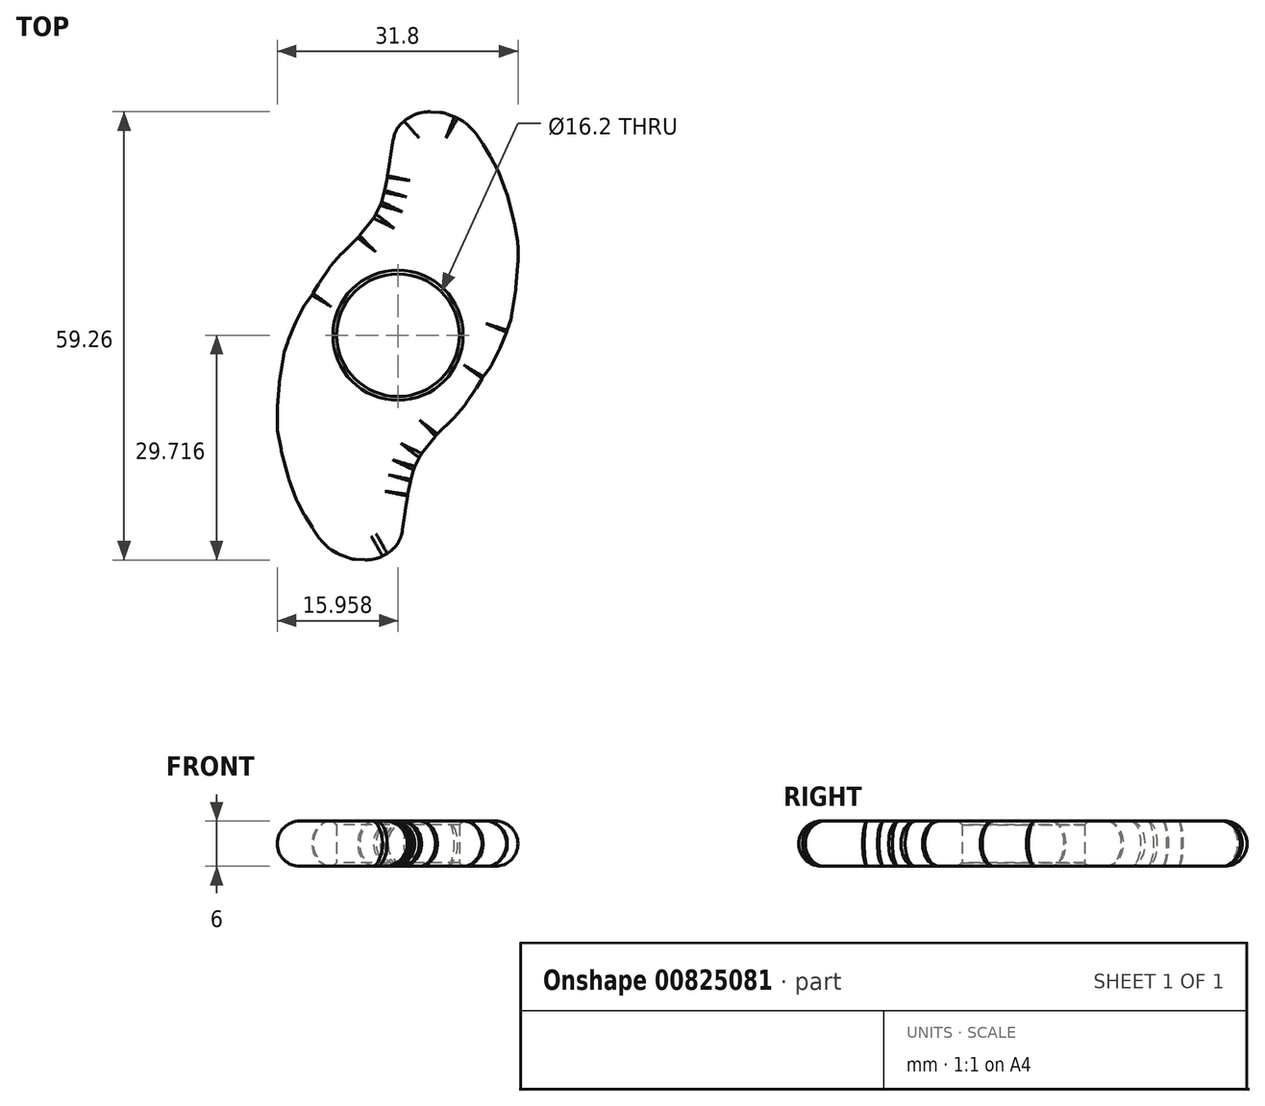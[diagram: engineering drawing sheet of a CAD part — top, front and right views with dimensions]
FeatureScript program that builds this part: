
annotation { "Feature Type Name" : "Feature", "Feature Type Description" : "" }
export const myFeature = defineFeature(function(context is Context, id is Id, definition is map)
    precondition{}
    {
        {
            var Q0;
            Q0=qCreatedBy(makeId("Top.planeOp"),FACE);
            var sketch = newSketch(context, id + "F0", { "sketchPlane" : qUnion([Q0])});
            skLineSegment(sketch, "E0", {"start": v(11.23, -5.5) * mm, "end": v(-11.23, 5.5) * mm});
            skLineSegment(sketch, "E1", {"start": v(11.23, -5.5) * mm, "end": v(12.39, -3.95) * mm});
            skLineSegment(sketch, "E2", {"start": v(12.39, -3.95) * mm, "end": v(13.48, -1.7) * mm});
            skLineSegment(sketch, "E3", {"start": v(13.48, -1.7) * mm, "end": v(14.46, 0.6) * mm});
            skLineSegment(sketch, "E4", {"start": v(14.46, 0.6) * mm, "end": v(15.04, 2.4) * mm});
            skLineSegment(sketch, "E5", {"start": v(15.04, 2.4) * mm, "end": v(15.61, 6.2) * mm});
            skLineSegment(sketch, "E6", {"start": v(15.61, 6.2) * mm, "end": v(15.9, 9.53) * mm});
            skLineSegment(sketch, "E7", {"start": v(15.9, 9.53) * mm, "end": v(15.9, 12.24) * mm});
            skLineSegment(sketch, "E8", {"start": v(15.9, 12.24) * mm, "end": v(15.38, 15.12) * mm});
            skLineSegment(sketch, "E9", {"start": v(15.38, 15.12) * mm, "end": v(14.4, 18.87) * mm});
            skLineSegment(sketch, "E10", {"start": v(14.4, 18.87) * mm, "end": v(13.3, 21.8) * mm});
            skLineSegment(sketch, "E11", {"start": v(13.3, 21.8) * mm, "end": v(12.27, 23.7) * mm});
            skLineSegment(sketch, "E12", {"start": v(12.27, 23.7) * mm, "end": v(11.23, 25.44) * mm});
            skLineSegment(sketch, "E13", {"start": v(11.23, 25.44) * mm, "end": v(10.25, 26.88) * mm});
            skLineSegment(sketch, "E14", {"start": v(10.25, 26.88) * mm, "end": v(9.1, 28.09) * mm});
            skLineSegment(sketch, "E15", {"start": v(9.1, 28.09) * mm, "end": v(7.72, 28.9) * mm});
            skLineSegment(sketch, "E16", {"start": v(7.72, 28.9) * mm, "end": v(6.05, 29.53) * mm});
            skLineSegment(sketch, "E17", {"start": v(6.05, 29.53) * mm, "end": v(3.92, 29.64) * mm});
            skLineSegment(sketch, "E18", {"start": v(3.92, 29.64) * mm, "end": v(2.42, 29.35) * mm});
            skLineSegment(sketch, "E19", {"start": v(2.42, 29.35) * mm, "end": v(1.1, 28.6) * mm});
            skLineSegment(sketch, "E20", {"start": v(1.1, 28.6) * mm, "end": v(0.12, 27.74) * mm});
            skLineSegment(sketch, "E21", {"start": v(0.12, 27.74) * mm, "end": v(-0.4, 26.7) * mm});
            skLineSegment(sketch, "E22", {"start": v(-0.4, 26.7) * mm, "end": v(-0.63, 25.78) * mm});
            skLineSegment(sketch, "E23", {"start": v(-0.63, 25.78) * mm, "end": v(-1.04, 23.13) * mm});
            skLineSegment(sketch, "E24", {"start": v(-1.04, 23.13) * mm, "end": v(-1.33, 21.06) * mm});
            skLineSegment(sketch, "E25", {"start": v(-1.33, 21.06) * mm, "end": v(-1.73, 19.1) * mm});
            skLineSegment(sketch, "E26", {"start": v(-1.73, 19.1) * mm, "end": v(-2.19, 17.48) * mm});
            skLineSegment(sketch, "E27", {"start": v(-2.19, 17.48) * mm, "end": v(-3, 15.81) * mm});
            skLineSegment(sketch, "E28", {"start": v(-3, 15.81) * mm, "end": v(-5.13, 13.1) * mm});
            skLineSegment(sketch, "E29", {"start": v(-5.13, 13.1) * mm, "end": v(-7.43, 10.86) * mm});
            skLineSegment(sketch, "E30", {"start": v(-7.43, 10.86) * mm, "end": v(-8.93, 9.13) * mm});
            skLineSegment(sketch, "E31", {"start": v(-8.93, 9.13) * mm, "end": v(-10.37, 6.94) * mm});
            skLineSegment(sketch, "E32", {"start": v(-10.37, 6.94) * mm, "end": v(-11.23, 5.5) * mm});
            skLineSegment(sketch, "E33", {"start": v(-11.23, 5.5) * mm, "end": v(-12.39, 3.95) * mm});
            skLineSegment(sketch, "E34", {"start": v(-12.39, 3.95) * mm, "end": v(-13.48, 1.7) * mm});
            skLineSegment(sketch, "E35", {"start": v(-13.48, 1.7) * mm, "end": v(-14.46, -0.6) * mm});
            skLineSegment(sketch, "E36", {"start": v(-14.46, -0.6) * mm, "end": v(-15.04, -2.4) * mm});
            skLineSegment(sketch, "E37", {"start": v(-15.04, -2.4) * mm, "end": v(-15.61, -6.2) * mm});
            skLineSegment(sketch, "E38", {"start": v(-15.61, -6.2) * mm, "end": v(-15.9, -9.53) * mm});
            skLineSegment(sketch, "E39", {"start": v(-15.9, -9.53) * mm, "end": v(-15.9, -12.24) * mm});
            skLineSegment(sketch, "E40", {"start": v(-15.9, -12.24) * mm, "end": v(-15.38, -15.12) * mm});
            skLineSegment(sketch, "E41", {"start": v(-15.38, -15.12) * mm, "end": v(-14.4, -18.87) * mm});
            skLineSegment(sketch, "E42", {"start": v(-14.4, -18.87) * mm, "end": v(-13.3, -21.8) * mm});
            skLineSegment(sketch, "E43", {"start": v(-13.3, -21.8) * mm, "end": v(-12.27, -23.7) * mm});
            skLineSegment(sketch, "E44", {"start": v(-12.27, -23.7) * mm, "end": v(-11.23, -25.44) * mm});
            skLineSegment(sketch, "E45", {"start": v(-11.23, -25.44) * mm, "end": v(-10.25, -26.88) * mm});
            skLineSegment(sketch, "E46", {"start": v(-10.25, -26.88) * mm, "end": v(-9.1, -28.09) * mm});
            skLineSegment(sketch, "E47", {"start": v(-9.1, -28.09) * mm, "end": v(-7.72, -28.9) * mm});
            skLineSegment(sketch, "E48", {"start": v(-7.72, -28.9) * mm, "end": v(-6.05, -29.53) * mm});
            skLineSegment(sketch, "E49", {"start": v(-6.05, -29.53) * mm, "end": v(-3.92, -29.64) * mm});
            skLineSegment(sketch, "E50", {"start": v(-3.92, -29.64) * mm, "end": v(-2.42, -29.35) * mm});
            skLineSegment(sketch, "E51", {"start": v(-2.42, -29.35) * mm, "end": v(-1.1, -28.6) * mm});
            skLineSegment(sketch, "E52", {"start": v(-1.1, -28.6) * mm, "end": v(-0.12, -27.74) * mm});
            skLineSegment(sketch, "E53", {"start": v(-0.12, -27.74) * mm, "end": v(0.4, -26.7) * mm});
            skLineSegment(sketch, "E54", {"start": v(0.4, -26.7) * mm, "end": v(0.63, -25.78) * mm});
            skLineSegment(sketch, "E55", {"start": v(0.63, -25.78) * mm, "end": v(1.04, -23.13) * mm});
            skLineSegment(sketch, "E56", {"start": v(1.04, -23.13) * mm, "end": v(1.33, -21.06) * mm});
            skLineSegment(sketch, "E57", {"start": v(1.33, -21.06) * mm, "end": v(1.73, -19.1) * mm});
            skLineSegment(sketch, "E58", {"start": v(1.73, -19.1) * mm, "end": v(2.19, -17.48) * mm});
            skLineSegment(sketch, "E59", {"start": v(2.19, -17.48) * mm, "end": v(3, -15.81) * mm});
            skLineSegment(sketch, "E60", {"start": v(3, -15.81) * mm, "end": v(5.13, -13.1) * mm});
            skLineSegment(sketch, "E61", {"start": v(5.13, -13.1) * mm, "end": v(7.43, -10.86) * mm});
            skLineSegment(sketch, "E62", {"start": v(7.43, -10.86) * mm, "end": v(8.93, -9.13) * mm});
            skLineSegment(sketch, "E63", {"start": v(8.93, -9.13) * mm, "end": v(10.37, -6.94) * mm});
            skLineSegment(sketch, "E64", {"start": v(10.37, -6.94) * mm, "end": v(11.23, -5.5) * mm});
            skLineSegment(sketch, "E65", {"start": v(0.06, 0.09) * mm, "end": v(-0.46, -1.07) * mm});
            skCircle(sketch, "E66", {"center": v(0.06, 0.09) * mm, "radius": 8.1 * mm});
            skSolve(sketch);
        }
        {
            var Q0;
            Q0 = qSketchRegion(id + "F0", true);
            var Q1;
            {var subQ0=sQuery(id+"F0.wireOp",EDGE,"E1");Q1=makeQuery(id+"F0.imprint","IMPRINT",FACE,{"disambiguationData":[TD([[makeQuery(id+"F0.imprint","IMPRINT",EDGE,{"derivedFrom":subQ0}),1.0]])]});}
            extrude(context, id + "F1", {"entities" : qUnion([Q0, Q1]), "depth" : 6 * mm, "offsetDistance" : 25 * mm});
        }
        {
            var Q0;
            Q0=makeQuery(id+"F1.opExtrude","CAP_EDGE",EDGE,{"disambiguationData":[OSD([sQuery(id+"F0.wireOp",EDGE,"E66")])],"isStart":false});
            var Q1;
            Q1=makeQuery(id+"F1.opExtrude","CAP_EDGE",EDGE,{"disambiguationData":[OSD([sQuery(id+"F0.wireOp",EDGE,"E66")])],"isStart":true});
            chamfer(context, id + "F2", {"entities" : qUnion([Q0, Q1]), "width" : 0.5 * mm, "tangentPropagation" : true});
        }
        {
            var Q0;
            Q0=makeQuery(id+"F1.opExtrude","CAP_EDGE",EDGE,{"disambiguationData":[OSD([sQuery(id+"F0.wireOp",EDGE,"E60")])],"isStart":false});
            var Q1;
            Q1=makeQuery(id+"F1.opExtrude","CAP_EDGE",EDGE,{"disambiguationData":[OSD([sQuery(id+"F0.wireOp",EDGE,"E61")])],"isStart":false});
            var Q2;
            Q2=makeQuery(id+"F1.opExtrude","CAP_EDGE",EDGE,{"disambiguationData":[OSD([sQuery(id+"F0.wireOp",EDGE,"E62")])],"isStart":false});
            var Q3;
            Q3=makeQuery(id+"F1.opExtrude","CAP_EDGE",EDGE,{"disambiguationData":[OSD([sQuery(id+"F0.wireOp",EDGE,"E63")])],"isStart":false});
            var Q4;
            Q4=makeQuery(id+"F1.opExtrude","CAP_EDGE",EDGE,{"disambiguationData":[OSD([sQuery(id+"F0.wireOp",EDGE,"E64")])],"isStart":false});
            var Q5;
            Q5=makeQuery(id+"F1.opExtrude","CAP_EDGE",EDGE,{"disambiguationData":[OSD([sQuery(id+"F0.wireOp",EDGE,"E1")])],"isStart":false});
            var Q6;
            Q6=makeQuery(id+"F1.opExtrude","CAP_EDGE",EDGE,{"disambiguationData":[OSD([sQuery(id+"F0.wireOp",EDGE,"E2")])],"isStart":false});
            var Q7;
            Q7=makeQuery(id+"F1.opExtrude","CAP_EDGE",EDGE,{"disambiguationData":[OSD([sQuery(id+"F0.wireOp",EDGE,"E3")])],"isStart":false});
            var Q8;
            Q8=makeQuery(id+"F1.opExtrude","CAP_EDGE",EDGE,{"disambiguationData":[OSD([sQuery(id+"F0.wireOp",EDGE,"E4")])],"isStart":false});
            var Q9;
            Q9=makeQuery(id+"F1.opExtrude","CAP_EDGE",EDGE,{"disambiguationData":[OSD([sQuery(id+"F0.wireOp",EDGE,"E5")])],"isStart":false});
            var Q10;
            Q10=makeQuery(id+"F1.opExtrude","CAP_EDGE",EDGE,{"disambiguationData":[OSD([sQuery(id+"F0.wireOp",EDGE,"E6")])],"isStart":false});
            var Q11;
            Q11=makeQuery(id+"F1.opExtrude","CAP_EDGE",EDGE,{"disambiguationData":[OSD([sQuery(id+"F0.wireOp",EDGE,"E7")])],"isStart":false});
            var Q12;
            Q12=makeQuery(id+"F1.opExtrude","CAP_EDGE",EDGE,{"disambiguationData":[OSD([sQuery(id+"F0.wireOp",EDGE,"E8")])],"isStart":false});
            var Q13;
            Q13=makeQuery(id+"F1.opExtrude","CAP_EDGE",EDGE,{"disambiguationData":[OSD([sQuery(id+"F0.wireOp",EDGE,"E9")])],"isStart":false});
            var Q14;
            Q14=makeQuery(id+"F1.opExtrude","CAP_EDGE",EDGE,{"disambiguationData":[OSD([sQuery(id+"F0.wireOp",EDGE,"E10")])],"isStart":false});
            var Q15;
            Q15=makeQuery(id+"F1.opExtrude","CAP_EDGE",EDGE,{"disambiguationData":[OSD([sQuery(id+"F0.wireOp",EDGE,"E11")])],"isStart":false});
            var Q16;
            Q16=makeQuery(id+"F1.opExtrude","CAP_EDGE",EDGE,{"disambiguationData":[OSD([sQuery(id+"F0.wireOp",EDGE,"E12")])],"isStart":false});
            var Q17;
            Q17=makeQuery(id+"F1.opExtrude","CAP_EDGE",EDGE,{"disambiguationData":[OSD([sQuery(id+"F0.wireOp",EDGE,"E13")])],"isStart":false});
            var Q18;
            Q18=makeQuery(id+"F1.opExtrude","CAP_EDGE",EDGE,{"disambiguationData":[OSD([sQuery(id+"F0.wireOp",EDGE,"E14")])],"isStart":false});
            var Q19;
            Q19=makeQuery(id+"F1.opExtrude","CAP_EDGE",EDGE,{"disambiguationData":[OSD([sQuery(id+"F0.wireOp",EDGE,"E15")])],"isStart":false});
            var Q20;
            Q20=makeQuery(id+"F1.opExtrude","CAP_EDGE",EDGE,{"disambiguationData":[OSD([sQuery(id+"F0.wireOp",EDGE,"E16")])],"isStart":false});
            var Q21;
            Q21=makeQuery(id+"F1.opExtrude","CAP_EDGE",EDGE,{"disambiguationData":[OSD([sQuery(id+"F0.wireOp",EDGE,"E17")])],"isStart":false});
            var Q22;
            Q22=makeQuery(id+"F1.opExtrude","CAP_EDGE",EDGE,{"disambiguationData":[OSD([sQuery(id+"F0.wireOp",EDGE,"E59")])],"isStart":false});
            var Q23;
            Q23=makeQuery(id+"F1.opExtrude","CAP_EDGE",EDGE,{"disambiguationData":[OSD([sQuery(id+"F0.wireOp",EDGE,"E58")])],"isStart":false});
            var Q24;
            Q24=makeQuery(id+"F1.opExtrude","CAP_EDGE",EDGE,{"disambiguationData":[OSD([sQuery(id+"F0.wireOp",EDGE,"E49")])],"isStart":false});
            var Q25;
            Q25=makeQuery(id+"F1.opExtrude","CAP_EDGE",EDGE,{"disambiguationData":[OSD([sQuery(id+"F0.wireOp",EDGE,"E51")])],"isStart":false});
            var Q26;
            Q26=makeQuery(id+"F1.opExtrude","CAP_EDGE",EDGE,{"disambiguationData":[OSD([sQuery(id+"F0.wireOp",EDGE,"E50")])],"isStart":false});
            var Q27;
            Q27=makeQuery(id+"F1.opExtrude","CAP_EDGE",EDGE,{"disambiguationData":[OSD([sQuery(id+"F0.wireOp",EDGE,"E52")])],"isStart":false});
            var Q28;
            Q28=makeQuery(id+"F1.opExtrude","CAP_EDGE",EDGE,{"disambiguationData":[OSD([sQuery(id+"F0.wireOp",EDGE,"E53")])],"isStart":false});
            var Q29;
            Q29=makeQuery(id+"F1.opExtrude","CAP_EDGE",EDGE,{"disambiguationData":[OSD([sQuery(id+"F0.wireOp",EDGE,"E54")])],"isStart":false});
            var Q30;
            Q30=makeQuery(id+"F1.opExtrude","CAP_EDGE",EDGE,{"disambiguationData":[OSD([sQuery(id+"F0.wireOp",EDGE,"E55")])],"isStart":false});
            var Q31;
            Q31=makeQuery(id+"F1.opExtrude","CAP_EDGE",EDGE,{"disambiguationData":[OSD([sQuery(id+"F0.wireOp",EDGE,"E56")])],"isStart":false});
            var Q32;
            Q32=makeQuery(id+"F1.opExtrude","CAP_EDGE",EDGE,{"disambiguationData":[OSD([sQuery(id+"F0.wireOp",EDGE,"E57")])],"isStart":false});
            var Q33;
            Q33=makeQuery(id+"F1.opExtrude","CAP_EDGE",EDGE,{"disambiguationData":[OSD([sQuery(id+"F0.wireOp",EDGE,"E48")])],"isStart":false});
            var Q34;
            Q34=makeQuery(id+"F1.opExtrude","CAP_EDGE",EDGE,{"disambiguationData":[OSD([sQuery(id+"F0.wireOp",EDGE,"E47")])],"isStart":false});
            var Q35;
            Q35=makeQuery(id+"F1.opExtrude","CAP_EDGE",EDGE,{"disambiguationData":[OSD([sQuery(id+"F0.wireOp",EDGE,"E46")])],"isStart":false});
            var Q36;
            Q36=makeQuery(id+"F1.opExtrude","CAP_EDGE",EDGE,{"disambiguationData":[OSD([sQuery(id+"F0.wireOp",EDGE,"E45")])],"isStart":false});
            var Q37;
            Q37=makeQuery(id+"F1.opExtrude","CAP_EDGE",EDGE,{"disambiguationData":[OSD([sQuery(id+"F0.wireOp",EDGE,"E44")])],"isStart":false});
            var Q38;
            Q38=makeQuery(id+"F1.opExtrude","CAP_EDGE",EDGE,{"disambiguationData":[OSD([sQuery(id+"F0.wireOp",EDGE,"E43")])],"isStart":false});
            var Q39;
            Q39=makeQuery(id+"F1.opExtrude","CAP_EDGE",EDGE,{"disambiguationData":[OSD([sQuery(id+"F0.wireOp",EDGE,"E42")])],"isStart":false});
            var Q40;
            Q40=makeQuery(id+"F1.opExtrude","CAP_EDGE",EDGE,{"disambiguationData":[OSD([sQuery(id+"F0.wireOp",EDGE,"E41")])],"isStart":false});
            var Q41;
            Q41=makeQuery(id+"F1.opExtrude","CAP_EDGE",EDGE,{"disambiguationData":[OSD([sQuery(id+"F0.wireOp",EDGE,"E40")])],"isStart":false});
            var Q42;
            Q42=makeQuery(id+"F1.opExtrude","CAP_EDGE",EDGE,{"disambiguationData":[OSD([sQuery(id+"F0.wireOp",EDGE,"E39")])],"isStart":false});
            var Q43;
            Q43=makeQuery(id+"F1.opExtrude","CAP_EDGE",EDGE,{"disambiguationData":[OSD([sQuery(id+"F0.wireOp",EDGE,"E38")])],"isStart":false});
            var Q44;
            Q44=makeQuery(id+"F1.opExtrude","CAP_EDGE",EDGE,{"disambiguationData":[OSD([sQuery(id+"F0.wireOp",EDGE,"E37")])],"isStart":false});
            var Q45;
            Q45=makeQuery(id+"F1.opExtrude","CAP_EDGE",EDGE,{"disambiguationData":[OSD([sQuery(id+"F0.wireOp",EDGE,"E36")])],"isStart":false});
            var Q46;
            Q46=makeQuery(id+"F1.opExtrude","CAP_EDGE",EDGE,{"disambiguationData":[OSD([sQuery(id+"F0.wireOp",EDGE,"E35")])],"isStart":false});
            var Q47;
            Q47=makeQuery(id+"F1.opExtrude","CAP_EDGE",EDGE,{"disambiguationData":[OSD([sQuery(id+"F0.wireOp",EDGE,"E34")])],"isStart":false});
            var Q48;
            Q48=makeQuery(id+"F1.opExtrude","CAP_EDGE",EDGE,{"disambiguationData":[OSD([sQuery(id+"F0.wireOp",EDGE,"E33")])],"isStart":false});
            var Q49;
            Q49=makeQuery(id+"F1.opExtrude","CAP_EDGE",EDGE,{"disambiguationData":[OSD([sQuery(id+"F0.wireOp",EDGE,"E32")])],"isStart":false});
            var Q50;
            Q50=makeQuery(id+"F1.opExtrude","CAP_EDGE",EDGE,{"disambiguationData":[OSD([sQuery(id+"F0.wireOp",EDGE,"E31")])],"isStart":false});
            var Q51;
            Q51=makeQuery(id+"F1.opExtrude","CAP_EDGE",EDGE,{"disambiguationData":[OSD([sQuery(id+"F0.wireOp",EDGE,"E30")])],"isStart":false});
            var Q52;
            Q52=makeQuery(id+"F1.opExtrude","CAP_EDGE",EDGE,{"disambiguationData":[OSD([sQuery(id+"F0.wireOp",EDGE,"E29")])],"isStart":false});
            var Q53;
            Q53=makeQuery(id+"F1.opExtrude","CAP_EDGE",EDGE,{"disambiguationData":[OSD([sQuery(id+"F0.wireOp",EDGE,"E28")])],"isStart":false});
            var Q54;
            Q54=makeQuery(id+"F1.opExtrude","CAP_EDGE",EDGE,{"disambiguationData":[OSD([sQuery(id+"F0.wireOp",EDGE,"E27")])],"isStart":false});
            var Q55;
            Q55=makeQuery(id+"F1.opExtrude","CAP_EDGE",EDGE,{"disambiguationData":[OSD([sQuery(id+"F0.wireOp",EDGE,"E26")])],"isStart":false});
            var Q56;
            Q56=makeQuery(id+"F1.opExtrude","CAP_EDGE",EDGE,{"disambiguationData":[OSD([sQuery(id+"F0.wireOp",EDGE,"E22")])],"isStart":false});
            var Q57;
            Q57=makeQuery(id+"F1.opExtrude","CAP_EDGE",EDGE,{"disambiguationData":[OSD([sQuery(id+"F0.wireOp",EDGE,"E21")])],"isStart":false});
            var Q58;
            Q58=makeQuery(id+"F1.opExtrude","CAP_EDGE",EDGE,{"disambiguationData":[OSD([sQuery(id+"F0.wireOp",EDGE,"E20")])],"isStart":false});
            var Q59;
            Q59=makeQuery(id+"F1.opExtrude","CAP_EDGE",EDGE,{"disambiguationData":[OSD([sQuery(id+"F0.wireOp",EDGE,"E19")])],"isStart":false});
            var Q60;
            Q60=makeQuery(id+"F1.opExtrude","CAP_EDGE",EDGE,{"disambiguationData":[OSD([sQuery(id+"F0.wireOp",EDGE,"E18")])],"isStart":false});
            var Q61;
            Q61=makeQuery(id+"F1.opExtrude","CAP_EDGE",EDGE,{"disambiguationData":[OSD([sQuery(id+"F0.wireOp",EDGE,"E25")])],"isStart":false});
            var Q62;
            Q62=makeQuery(id+"F1.opExtrude","CAP_EDGE",EDGE,{"disambiguationData":[OSD([sQuery(id+"F0.wireOp",EDGE,"E24")])],"isStart":false});
            var Q63;
            Q63=makeQuery(id+"F1.opExtrude","CAP_EDGE",EDGE,{"disambiguationData":[OSD([sQuery(id+"F0.wireOp",EDGE,"E23")])],"isStart":false});
            var Q64;
            Q64=makeQuery(id+"F1.opExtrude","CAP_EDGE",EDGE,{"disambiguationData":[OSD([sQuery(id+"F0.wireOp",EDGE,"E26")])],"isStart":true});
            var Q65;
            Q65=makeQuery(id+"F1.opExtrude","CAP_EDGE",EDGE,{"disambiguationData":[OSD([sQuery(id+"F0.wireOp",EDGE,"E25")])],"isStart":true});
            var Q66;
            Q66=makeQuery(id+"F1.opExtrude","CAP_EDGE",EDGE,{"disambiguationData":[OSD([sQuery(id+"F0.wireOp",EDGE,"E24")])],"isStart":true});
            var Q67;
            Q67=makeQuery(id+"F1.opExtrude","CAP_EDGE",EDGE,{"disambiguationData":[OSD([sQuery(id+"F0.wireOp",EDGE,"E23")])],"isStart":true});
            var Q68;
            Q68=makeQuery(id+"F1.opExtrude","CAP_EDGE",EDGE,{"disambiguationData":[OSD([sQuery(id+"F0.wireOp",EDGE,"E22")])],"isStart":true});
            var Q69;
            Q69=makeQuery(id+"F1.opExtrude","CAP_EDGE",EDGE,{"disambiguationData":[OSD([sQuery(id+"F0.wireOp",EDGE,"E21")])],"isStart":true});
            var Q70;
            Q70=makeQuery(id+"F1.opExtrude","CAP_EDGE",EDGE,{"disambiguationData":[OSD([sQuery(id+"F0.wireOp",EDGE,"E20")])],"isStart":true});
            var Q71;
            Q71=makeQuery(id+"F1.opExtrude","CAP_EDGE",EDGE,{"disambiguationData":[OSD([sQuery(id+"F0.wireOp",EDGE,"E19")])],"isStart":true});
            var Q72;
            Q72=makeQuery(id+"F1.opExtrude","CAP_EDGE",EDGE,{"disambiguationData":[OSD([sQuery(id+"F0.wireOp",EDGE,"E27")])],"isStart":true});
            var Q73;
            Q73=makeQuery(id+"F1.opExtrude","CAP_EDGE",EDGE,{"disambiguationData":[OSD([sQuery(id+"F0.wireOp",EDGE,"E28")])],"isStart":true});
            var Q74;
            Q74=makeQuery(id+"F1.opExtrude","CAP_EDGE",EDGE,{"disambiguationData":[OSD([sQuery(id+"F0.wireOp",EDGE,"E29")])],"isStart":true});
            var Q75;
            Q75=makeQuery(id+"F1.opExtrude","CAP_EDGE",EDGE,{"disambiguationData":[OSD([sQuery(id+"F0.wireOp",EDGE,"E30")])],"isStart":true});
            var Q76;
            Q76=makeQuery(id+"F1.opExtrude","CAP_EDGE",EDGE,{"disambiguationData":[OSD([sQuery(id+"F0.wireOp",EDGE,"E31")])],"isStart":true});
            var Q77;
            Q77=makeQuery(id+"F1.opExtrude","CAP_EDGE",EDGE,{"disambiguationData":[OSD([sQuery(id+"F0.wireOp",EDGE,"E32")])],"isStart":true});
            var Q78;
            Q78=makeQuery(id+"F1.opExtrude","CAP_EDGE",EDGE,{"disambiguationData":[OSD([sQuery(id+"F0.wireOp",EDGE,"E33")])],"isStart":true});
            var Q79;
            Q79=makeQuery(id+"F1.opExtrude","CAP_EDGE",EDGE,{"disambiguationData":[OSD([sQuery(id+"F0.wireOp",EDGE,"E34")])],"isStart":true});
            var Q80;
            Q80=makeQuery(id+"F1.opExtrude","CAP_EDGE",EDGE,{"disambiguationData":[OSD([sQuery(id+"F0.wireOp",EDGE,"E35")])],"isStart":true});
            var Q81;
            Q81=makeQuery(id+"F1.opExtrude","CAP_EDGE",EDGE,{"disambiguationData":[OSD([sQuery(id+"F0.wireOp",EDGE,"E37")])],"isStart":true});
            var Q82;
            Q82=makeQuery(id+"F1.opExtrude","CAP_EDGE",EDGE,{"disambiguationData":[OSD([sQuery(id+"F0.wireOp",EDGE,"E36")])],"isStart":true});
            var Q83;
            Q83=makeQuery(id+"F1.opExtrude","CAP_EDGE",EDGE,{"disambiguationData":[OSD([sQuery(id+"F0.wireOp",EDGE,"E39")])],"isStart":true});
            var Q84;
            Q84=makeQuery(id+"F1.opExtrude","CAP_EDGE",EDGE,{"disambiguationData":[OSD([sQuery(id+"F0.wireOp",EDGE,"E38")])],"isStart":true});
            var Q85;
            Q85=makeQuery(id+"F1.opExtrude","CAP_EDGE",EDGE,{"disambiguationData":[OSD([sQuery(id+"F0.wireOp",EDGE,"E40")])],"isStart":true});
            var Q86;
            Q86=makeQuery(id+"F1.opExtrude","CAP_EDGE",EDGE,{"disambiguationData":[OSD([sQuery(id+"F0.wireOp",EDGE,"E41")])],"isStart":true});
            var Q87;
            Q87=makeQuery(id+"F1.opExtrude","CAP_EDGE",EDGE,{"disambiguationData":[OSD([sQuery(id+"F0.wireOp",EDGE,"E42")])],"isStart":true});
            var Q88;
            Q88=makeQuery(id+"F1.opExtrude","CAP_EDGE",EDGE,{"disambiguationData":[OSD([sQuery(id+"F0.wireOp",EDGE,"E43")])],"isStart":true});
            var Q89;
            Q89=makeQuery(id+"F1.opExtrude","CAP_EDGE",EDGE,{"disambiguationData":[OSD([sQuery(id+"F0.wireOp",EDGE,"E44")])],"isStart":true});
            var Q90;
            Q90=makeQuery(id+"F1.opExtrude","CAP_EDGE",EDGE,{"disambiguationData":[OSD([sQuery(id+"F0.wireOp",EDGE,"E45")])],"isStart":true});
            var Q91;
            Q91=makeQuery(id+"F1.opExtrude","CAP_EDGE",EDGE,{"disambiguationData":[OSD([sQuery(id+"F0.wireOp",EDGE,"E46")])],"isStart":true});
            var Q92;
            Q92=makeQuery(id+"F1.opExtrude","CAP_EDGE",EDGE,{"disambiguationData":[OSD([sQuery(id+"F0.wireOp",EDGE,"E47")])],"isStart":true});
            var Q93;
            Q93=makeQuery(id+"F1.opExtrude","CAP_EDGE",EDGE,{"disambiguationData":[OSD([sQuery(id+"F0.wireOp",EDGE,"E48")])],"isStart":true});
            var Q94;
            Q94=makeQuery(id+"F1.opExtrude","CAP_EDGE",EDGE,{"disambiguationData":[OSD([sQuery(id+"F0.wireOp",EDGE,"E49")])],"isStart":true});
            var Q95;
            Q95=makeQuery(id+"F1.opExtrude","CAP_EDGE",EDGE,{"disambiguationData":[OSD([sQuery(id+"F0.wireOp",EDGE,"E50")])],"isStart":true});
            var Q96;
            Q96=makeQuery(id+"F1.opExtrude","CAP_EDGE",EDGE,{"disambiguationData":[OSD([sQuery(id+"F0.wireOp",EDGE,"E51")])],"isStart":true});
            var Q97;
            Q97=makeQuery(id+"F1.opExtrude","CAP_EDGE",EDGE,{"disambiguationData":[OSD([sQuery(id+"F0.wireOp",EDGE,"E52")])],"isStart":true});
            var Q98;
            Q98=makeQuery(id+"F1.opExtrude","CAP_EDGE",EDGE,{"disambiguationData":[OSD([sQuery(id+"F0.wireOp",EDGE,"E53")])],"isStart":true});
            var Q99;
            Q99=makeQuery(id+"F1.opExtrude","CAP_EDGE",EDGE,{"disambiguationData":[OSD([sQuery(id+"F0.wireOp",EDGE,"E54")])],"isStart":true});
            var Q100;
            Q100=makeQuery(id+"F1.opExtrude","CAP_EDGE",EDGE,{"disambiguationData":[OSD([sQuery(id+"F0.wireOp",EDGE,"E55")])],"isStart":true});
            var Q101;
            Q101=makeQuery(id+"F1.opExtrude","CAP_EDGE",EDGE,{"disambiguationData":[OSD([sQuery(id+"F0.wireOp",EDGE,"E56")])],"isStart":true});
            var Q102;
            Q102=makeQuery(id+"F1.opExtrude","CAP_EDGE",EDGE,{"disambiguationData":[OSD([sQuery(id+"F0.wireOp",EDGE,"E57")])],"isStart":true});
            var Q103;
            Q103=makeQuery(id+"F1.opExtrude","CAP_EDGE",EDGE,{"disambiguationData":[OSD([sQuery(id+"F0.wireOp",EDGE,"E59")])],"isStart":true});
            var Q104;
            Q104=makeQuery(id+"F1.opExtrude","CAP_EDGE",EDGE,{"disambiguationData":[OSD([sQuery(id+"F0.wireOp",EDGE,"E60")])],"isStart":true});
            var Q105;
            Q105=makeQuery(id+"F1.opExtrude","CAP_EDGE",EDGE,{"disambiguationData":[OSD([sQuery(id+"F0.wireOp",EDGE,"E61")])],"isStart":true});
            var Q106;
            Q106=makeQuery(id+"F1.opExtrude","CAP_EDGE",EDGE,{"disambiguationData":[OSD([sQuery(id+"F0.wireOp",EDGE,"E62")])],"isStart":true});
            var Q107;
            Q107=makeQuery(id+"F1.opExtrude","CAP_EDGE",EDGE,{"disambiguationData":[OSD([sQuery(id+"F0.wireOp",EDGE,"E63")])],"isStart":true});
            var Q108;
            Q108=makeQuery(id+"F1.opExtrude","CAP_EDGE",EDGE,{"disambiguationData":[OSD([sQuery(id+"F0.wireOp",EDGE,"E64")])],"isStart":true});
            var Q109;
            Q109=makeQuery(id+"F1.opExtrude","CAP_EDGE",EDGE,{"disambiguationData":[OSD([sQuery(id+"F0.wireOp",EDGE,"E1")])],"isStart":true});
            var Q110;
            Q110=makeQuery(id+"F1.opExtrude","CAP_EDGE",EDGE,{"disambiguationData":[OSD([sQuery(id+"F0.wireOp",EDGE,"E2")])],"isStart":true});
            var Q111;
            Q111=makeQuery(id+"F1.opExtrude","CAP_EDGE",EDGE,{"disambiguationData":[OSD([sQuery(id+"F0.wireOp",EDGE,"E3")])],"isStart":true});
            var Q112;
            Q112=makeQuery(id+"F1.opExtrude","CAP_EDGE",EDGE,{"disambiguationData":[OSD([sQuery(id+"F0.wireOp",EDGE,"E4")])],"isStart":true});
            var Q113;
            Q113=makeQuery(id+"F1.opExtrude","CAP_EDGE",EDGE,{"disambiguationData":[OSD([sQuery(id+"F0.wireOp",EDGE,"E5")])],"isStart":true});
            var Q114;
            Q114=makeQuery(id+"F1.opExtrude","CAP_EDGE",EDGE,{"disambiguationData":[OSD([sQuery(id+"F0.wireOp",EDGE,"E6")])],"isStart":true});
            var Q115;
            Q115=makeQuery(id+"F1.opExtrude","CAP_EDGE",EDGE,{"disambiguationData":[OSD([sQuery(id+"F0.wireOp",EDGE,"E7")])],"isStart":true});
            var Q116;
            Q116=makeQuery(id+"F1.opExtrude","CAP_EDGE",EDGE,{"disambiguationData":[OSD([sQuery(id+"F0.wireOp",EDGE,"E8")])],"isStart":true});
            var Q117;
            Q117=makeQuery(id+"F1.opExtrude","CAP_EDGE",EDGE,{"disambiguationData":[OSD([sQuery(id+"F0.wireOp",EDGE,"E9")])],"isStart":true});
            var Q118;
            Q118=makeQuery(id+"F1.opExtrude","CAP_EDGE",EDGE,{"disambiguationData":[OSD([sQuery(id+"F0.wireOp",EDGE,"E10")])],"isStart":true});
            var Q119;
            Q119=makeQuery(id+"F1.opExtrude","CAP_EDGE",EDGE,{"disambiguationData":[OSD([sQuery(id+"F0.wireOp",EDGE,"E11")])],"isStart":true});
            var Q120;
            Q120=makeQuery(id+"F1.opExtrude","CAP_EDGE",EDGE,{"disambiguationData":[OSD([sQuery(id+"F0.wireOp",EDGE,"E12")])],"isStart":true});
            var Q121;
            Q121=makeQuery(id+"F1.opExtrude","CAP_EDGE",EDGE,{"disambiguationData":[OSD([sQuery(id+"F0.wireOp",EDGE,"E13")])],"isStart":true});
            var Q122;
            Q122=makeQuery(id+"F1.opExtrude","CAP_EDGE",EDGE,{"disambiguationData":[OSD([sQuery(id+"F0.wireOp",EDGE,"E14")])],"isStart":true});
            var Q123;
            Q123=makeQuery(id+"F1.opExtrude","CAP_EDGE",EDGE,{"disambiguationData":[OSD([sQuery(id+"F0.wireOp",EDGE,"E15")])],"isStart":true});
            var Q124;
            Q124=makeQuery(id+"F1.opExtrude","CAP_EDGE",EDGE,{"disambiguationData":[OSD([sQuery(id+"F0.wireOp",EDGE,"E16")])],"isStart":true});
            var Q125;
            Q125=makeQuery(id+"F1.opExtrude","CAP_EDGE",EDGE,{"disambiguationData":[OSD([sQuery(id+"F0.wireOp",EDGE,"E17")])],"isStart":true});
            var Q126;
            Q126=makeQuery(id+"F1.opExtrude","CAP_EDGE",EDGE,{"disambiguationData":[OSD([sQuery(id+"F0.wireOp",EDGE,"E18")])],"isStart":true});
            fillet(context, id + "F3", {"entities" : qUnion([Q0, Q1, Q2, Q3, Q4, Q5, Q6, Q7, Q8, Q9, Q10, Q11, Q12, Q13, Q14, Q15, Q16, Q17, Q18, Q19, Q20, Q21, Q22, Q23, Q24, Q25, Q26, Q27, Q28, Q29, Q30, Q31, Q32, Q33, Q34, Q35, Q36, Q37, Q38, Q39, Q40, Q41, Q42, Q43, Q44, Q45, Q46, Q47, Q48, Q49, Q50, Q51, Q52, Q53, Q54, Q55, Q56, Q57, Q58, Q59, Q60, Q61, Q62, Q63, Q64, Q65, Q66, Q67, Q68, Q69, Q70, Q71, Q72, Q73, Q74, Q75, Q76, Q77, Q78, Q79, Q80, Q81, Q82, Q83, Q84, Q85, Q86, Q87, Q88, Q89, Q90, Q91, Q92, Q93, Q94, Q95, Q96, Q97, Q98, Q99, Q100, Q101, Q102, Q103, Q104, Q105, Q106, Q107, Q108, Q109, Q110, Q111, Q112, Q113, Q114, Q115, Q116, Q117, Q118, Q119, Q120, Q121, Q122, Q123, Q124, Q125, Q126]), "radius" : 3 * mm, "tangentPropagation" : true, "allowEdgeOverflow" : false});
        }
        {
            var Q0;
            Q0=makeQuery(id+"F3.opFillet","BLEND_EDGE",EDGE,{"blendedFrom":[makeQuery(id+"F1.opExtrude","CAP_EDGE",EDGE,{"disambiguationData":[OSD([sQuery(id+"F0.wireOp",EDGE,"E25")])],"isStart":true}),makeQuery(id+"F1.opExtrude","CAP_EDGE",EDGE,{"disambiguationData":[OSD([sQuery(id+"F0.wireOp",EDGE,"E26")])],"isStart":true})],"blendedInto":[]});
            var Q1;
            Q1=makeQuery(id+"F3.opFillet","BLEND_EDGE",EDGE,{"blendedFrom":[makeQuery(id+"F1.opExtrude","CAP_EDGE",EDGE,{"disambiguationData":[OSD([sQuery(id+"F0.wireOp",EDGE,"E24")])],"isStart":true}),makeQuery(id+"F1.opExtrude","CAP_EDGE",EDGE,{"disambiguationData":[OSD([sQuery(id+"F0.wireOp",EDGE,"E25")])],"isStart":true})],"blendedInto":[]});
            var Q2;
            Q2=makeQuery(id+"F3.opFillet","BLEND_EDGE",EDGE,{"blendedFrom":[makeQuery(id+"F1.opExtrude","CAP_EDGE",EDGE,{"disambiguationData":[OSD([sQuery(id+"F0.wireOp",EDGE,"E26")])],"isStart":true}),makeQuery(id+"F1.opExtrude","CAP_EDGE",EDGE,{"disambiguationData":[OSD([sQuery(id+"F0.wireOp",EDGE,"E27")])],"isStart":true})],"blendedInto":[]});
            var Q3;
            Q3=makeQuery(id+"F3.opFillet","BLEND_EDGE",EDGE,{"blendedFrom":[makeQuery(id+"F1.opExtrude","CAP_EDGE",EDGE,{"disambiguationData":[OSD([sQuery(id+"F0.wireOp",EDGE,"E23")])],"isStart":true}),makeQuery(id+"F1.opExtrude","CAP_EDGE",EDGE,{"disambiguationData":[OSD([sQuery(id+"F0.wireOp",EDGE,"E24")])],"isStart":true})],"blendedInto":[]});
            var Q4;
            Q4=makeQuery(id+"F3.opFillet","BLEND_EDGE",EDGE,{"blendedFrom":[makeQuery(id+"F1.opExtrude","CAP_EDGE",EDGE,{"disambiguationData":[OSD([sQuery(id+"F0.wireOp",EDGE,"E27")])],"isStart":true}),makeQuery(id+"F1.opExtrude","CAP_EDGE",EDGE,{"disambiguationData":[OSD([sQuery(id+"F0.wireOp",EDGE,"E28")])],"isStart":true})],"blendedInto":[]});
            var Q5;
            Q5=makeQuery(id+"F3.opFillet","BLEND_EDGE",EDGE,{"blendedFrom":[makeQuery(id+"F1.opExtrude","CAP_EDGE",EDGE,{"disambiguationData":[OSD([sQuery(id+"F0.wireOp",EDGE,"E22")])],"isStart":true}),makeQuery(id+"F1.opExtrude","CAP_EDGE",EDGE,{"disambiguationData":[OSD([sQuery(id+"F0.wireOp",EDGE,"E23")])],"isStart":true})],"blendedInto":[]});
            var Q6;
            Q6=makeQuery(id+"F3.opFillet","BLEND_EDGE",EDGE,{"blendedFrom":[makeQuery(id+"F1.opExtrude","CAP_EDGE",EDGE,{"disambiguationData":[OSD([sQuery(id+"F0.wireOp",EDGE,"E29")])],"isStart":true}),makeQuery(id+"F1.opExtrude","CAP_EDGE",EDGE,{"disambiguationData":[OSD([sQuery(id+"F0.wireOp",EDGE,"E30")])],"isStart":true})],"blendedInto":[]});
            var Q7;
            Q7=makeQuery(id+"F3.opFillet","BLEND_EDGE",EDGE,{"blendedFrom":[makeQuery(id+"F1.opExtrude","CAP_EDGE",EDGE,{"disambiguationData":[OSD([sQuery(id+"F0.wireOp",EDGE,"E28")])],"isStart":true}),makeQuery(id+"F1.opExtrude","CAP_EDGE",EDGE,{"disambiguationData":[OSD([sQuery(id+"F0.wireOp",EDGE,"E29")])],"isStart":true})],"blendedInto":[]});
            var Q8;
            Q8=makeQuery(id+"F3.opFillet","BLEND_EDGE",EDGE,{"blendedFrom":[makeQuery(id+"F1.opExtrude","CAP_EDGE",EDGE,{"disambiguationData":[OSD([sQuery(id+"F0.wireOp",EDGE,"E31")])],"isStart":true}),makeQuery(id+"F1.opExtrude","CAP_EDGE",EDGE,{"disambiguationData":[OSD([sQuery(id+"F0.wireOp",EDGE,"E32")])],"isStart":true})],"blendedInto":[]});
            var Q9;
            Q9=makeQuery(id+"F3.opFillet","BLEND_EDGE",EDGE,{"blendedFrom":[makeQuery(id+"F1.opExtrude","CAP_EDGE",EDGE,{"disambiguationData":[OSD([sQuery(id+"F0.wireOp",EDGE,"E30")])],"isStart":true}),makeQuery(id+"F1.opExtrude","CAP_EDGE",EDGE,{"disambiguationData":[OSD([sQuery(id+"F0.wireOp",EDGE,"E31")])],"isStart":true})],"blendedInto":[]});
            var Q10;
            Q10=makeQuery(id+"F3.opFillet","BLEND_EDGE",EDGE,{"blendedFrom":[makeQuery(id+"F1.opExtrude","CAP_EDGE",EDGE,{"disambiguationData":[OSD([sQuery(id+"F0.wireOp",EDGE,"E32")])],"isStart":true}),makeQuery(id+"F1.opExtrude","CAP_EDGE",EDGE,{"disambiguationData":[OSD([sQuery(id+"F0.wireOp",EDGE,"E33")])],"isStart":true})],"blendedInto":[]});
            var Q11;
            Q11=makeQuery(id+"F3.opFillet","BLEND_EDGE",EDGE,{"blendedFrom":[makeQuery(id+"F1.opExtrude","CAP_EDGE",EDGE,{"disambiguationData":[OSD([sQuery(id+"F0.wireOp",EDGE,"E33")])],"isStart":true}),makeQuery(id+"F1.opExtrude","CAP_EDGE",EDGE,{"disambiguationData":[OSD([sQuery(id+"F0.wireOp",EDGE,"E34")])],"isStart":true})],"blendedInto":[]});
            var Q12;
            Q12=makeQuery(id+"F3.opFillet","BLEND_EDGE",EDGE,{"blendedFrom":[makeQuery(id+"F1.opExtrude","CAP_EDGE",EDGE,{"disambiguationData":[OSD([sQuery(id+"F0.wireOp",EDGE,"E34")])],"isStart":true}),makeQuery(id+"F1.opExtrude","CAP_EDGE",EDGE,{"disambiguationData":[OSD([sQuery(id+"F0.wireOp",EDGE,"E35")])],"isStart":true})],"blendedInto":[]});
            var Q13;
            Q13=makeQuery(id+"F3.opFillet","BLEND_EDGE",EDGE,{"blendedFrom":[makeQuery(id+"F1.opExtrude","CAP_EDGE",EDGE,{"disambiguationData":[OSD([sQuery(id+"F0.wireOp",EDGE,"E35")])],"isStart":true}),makeQuery(id+"F1.opExtrude","CAP_EDGE",EDGE,{"disambiguationData":[OSD([sQuery(id+"F0.wireOp",EDGE,"E36")])],"isStart":true})],"blendedInto":[]});
            var Q14;
            Q14=makeQuery(id+"F3.opFillet","BLEND_EDGE",EDGE,{"blendedFrom":[makeQuery(id+"F1.opExtrude","CAP_EDGE",EDGE,{"disambiguationData":[OSD([sQuery(id+"F0.wireOp",EDGE,"E36")])],"isStart":true}),makeQuery(id+"F1.opExtrude","CAP_EDGE",EDGE,{"disambiguationData":[OSD([sQuery(id+"F0.wireOp",EDGE,"E37")])],"isStart":true})],"blendedInto":[]});
            var Q15;
            Q15=makeQuery(id+"F3.opFillet","BLEND_EDGE",EDGE,{"blendedFrom":[makeQuery(id+"F1.opExtrude","CAP_EDGE",EDGE,{"disambiguationData":[OSD([sQuery(id+"F0.wireOp",EDGE,"E37")])],"isStart":true}),makeQuery(id+"F1.opExtrude","CAP_EDGE",EDGE,{"disambiguationData":[OSD([sQuery(id+"F0.wireOp",EDGE,"E38")])],"isStart":true})],"blendedInto":[]});
            var Q16;
            Q16=makeQuery(id+"F3.opFillet","BLEND_EDGE",EDGE,{"blendedFrom":[makeQuery(id+"F1.opExtrude","CAP_EDGE",EDGE,{"disambiguationData":[OSD([sQuery(id+"F0.wireOp",EDGE,"E38")])],"isStart":true}),makeQuery(id+"F1.opExtrude","CAP_EDGE",EDGE,{"disambiguationData":[OSD([sQuery(id+"F0.wireOp",EDGE,"E39")])],"isStart":true})],"blendedInto":[]});
            var Q17;
            Q17=makeQuery(id+"F3.opFillet","BLEND_EDGE",EDGE,{"blendedFrom":[makeQuery(id+"F1.opExtrude","CAP_EDGE",EDGE,{"disambiguationData":[OSD([sQuery(id+"F0.wireOp",EDGE,"E39")])],"isStart":true}),makeQuery(id+"F1.opExtrude","CAP_EDGE",EDGE,{"disambiguationData":[OSD([sQuery(id+"F0.wireOp",EDGE,"E40")])],"isStart":true})],"blendedInto":[]});
            var Q18;
            Q18=makeQuery(id+"F3.opFillet","BLEND_EDGE",EDGE,{"blendedFrom":[makeQuery(id+"F1.opExtrude","CAP_EDGE",EDGE,{"disambiguationData":[OSD([sQuery(id+"F0.wireOp",EDGE,"E40")])],"isStart":true}),makeQuery(id+"F1.opExtrude","CAP_EDGE",EDGE,{"disambiguationData":[OSD([sQuery(id+"F0.wireOp",EDGE,"E41")])],"isStart":true})],"blendedInto":[]});
            var Q19;
            Q19=makeQuery(id+"F3.opFillet","BLEND_EDGE",EDGE,{"blendedFrom":[makeQuery(id+"F1.opExtrude","CAP_EDGE",EDGE,{"disambiguationData":[OSD([sQuery(id+"F0.wireOp",EDGE,"E41")])],"isStart":true}),makeQuery(id+"F1.opExtrude","CAP_EDGE",EDGE,{"disambiguationData":[OSD([sQuery(id+"F0.wireOp",EDGE,"E42")])],"isStart":true})],"blendedInto":[]});
            var Q20;
            Q20=makeQuery(id+"F3.opFillet","BLEND_EDGE",EDGE,{"blendedFrom":[makeQuery(id+"F1.opExtrude","CAP_EDGE",EDGE,{"disambiguationData":[OSD([sQuery(id+"F0.wireOp",EDGE,"E42")])],"isStart":true}),makeQuery(id+"F1.opExtrude","CAP_EDGE",EDGE,{"disambiguationData":[OSD([sQuery(id+"F0.wireOp",EDGE,"E43")])],"isStart":true})],"blendedInto":[]});
            var Q21;
            Q21=makeQuery(id+"F3.opFillet","BLEND_EDGE",EDGE,{"blendedFrom":[makeQuery(id+"F1.opExtrude","CAP_EDGE",EDGE,{"disambiguationData":[OSD([sQuery(id+"F0.wireOp",EDGE,"E43")])],"isStart":true}),makeQuery(id+"F1.opExtrude","CAP_EDGE",EDGE,{"disambiguationData":[OSD([sQuery(id+"F0.wireOp",EDGE,"E44")])],"isStart":true})],"blendedInto":[]});
            var Q22;
            Q22=makeQuery(id+"F3.opFillet","BLEND_EDGE",EDGE,{"blendedFrom":[makeQuery(id+"F1.opExtrude","CAP_EDGE",EDGE,{"disambiguationData":[OSD([sQuery(id+"F0.wireOp",EDGE,"E44")])],"isStart":true}),makeQuery(id+"F1.opExtrude","CAP_EDGE",EDGE,{"disambiguationData":[OSD([sQuery(id+"F0.wireOp",EDGE,"E45")])],"isStart":true})],"blendedInto":[]});
            var Q23;
            Q23=makeQuery(id+"F3.opFillet","BLEND_EDGE",EDGE,{"blendedFrom":[makeQuery(id+"F1.opExtrude","CAP_EDGE",EDGE,{"disambiguationData":[OSD([sQuery(id+"F0.wireOp",EDGE,"E45")])],"isStart":true}),makeQuery(id+"F1.opExtrude","CAP_EDGE",EDGE,{"disambiguationData":[OSD([sQuery(id+"F0.wireOp",EDGE,"E46")])],"isStart":true})],"blendedInto":[]});
            var Q24;
            Q24=makeQuery(id+"F3.opFillet","BLEND_EDGE",EDGE,{"blendedFrom":[makeQuery(id+"F1.opExtrude","CAP_EDGE",EDGE,{"disambiguationData":[OSD([sQuery(id+"F0.wireOp",EDGE,"E46")])],"isStart":true}),makeQuery(id+"F1.opExtrude","CAP_EDGE",EDGE,{"disambiguationData":[OSD([sQuery(id+"F0.wireOp",EDGE,"E47")])],"isStart":true})],"blendedInto":[]});
            var Q25;
            Q25=makeQuery(id+"F3.opFillet","BLEND_EDGE",EDGE,{"blendedFrom":[makeQuery(id+"F1.opExtrude","CAP_EDGE",EDGE,{"disambiguationData":[OSD([sQuery(id+"F0.wireOp",EDGE,"E47")])],"isStart":true}),makeQuery(id+"F1.opExtrude","CAP_EDGE",EDGE,{"disambiguationData":[OSD([sQuery(id+"F0.wireOp",EDGE,"E48")])],"isStart":true})],"blendedInto":[]});
            var Q26;
            Q26=makeQuery(id+"F3.opFillet","BLEND_EDGE",EDGE,{"blendedFrom":[makeQuery(id+"F1.opExtrude","CAP_EDGE",EDGE,{"disambiguationData":[OSD([sQuery(id+"F0.wireOp",EDGE,"E48")])],"isStart":true}),makeQuery(id+"F1.opExtrude","CAP_EDGE",EDGE,{"disambiguationData":[OSD([sQuery(id+"F0.wireOp",EDGE,"E49")])],"isStart":true})],"blendedInto":[]});
            var Q27;
            Q27=makeQuery(id+"F3.opFillet","BLEND_EDGE",EDGE,{"blendedFrom":[makeQuery(id+"F1.opExtrude","CAP_EDGE",EDGE,{"disambiguationData":[OSD([sQuery(id+"F0.wireOp",EDGE,"E49")])],"isStart":true}),makeQuery(id+"F1.opExtrude","CAP_EDGE",EDGE,{"disambiguationData":[OSD([sQuery(id+"F0.wireOp",EDGE,"E50")])],"isStart":true})],"blendedInto":[]});
            var Q28;
            Q28=makeQuery(id+"F3.opFillet","BLEND_EDGE",EDGE,{"blendedFrom":[makeQuery(id+"F1.opExtrude","CAP_EDGE",EDGE,{"disambiguationData":[OSD([sQuery(id+"F0.wireOp",EDGE,"E50")])],"isStart":true}),makeQuery(id+"F1.opExtrude","CAP_EDGE",EDGE,{"disambiguationData":[OSD([sQuery(id+"F0.wireOp",EDGE,"E51")])],"isStart":true})],"blendedInto":[]});
            var Q29;
            Q29=makeQuery(id+"F3.opFillet","BLEND_EDGE",EDGE,{"blendedFrom":[makeQuery(id+"F1.opExtrude","CAP_EDGE",EDGE,{"disambiguationData":[OSD([sQuery(id+"F0.wireOp",EDGE,"E51")])],"isStart":true}),makeQuery(id+"F1.opExtrude","CAP_EDGE",EDGE,{"disambiguationData":[OSD([sQuery(id+"F0.wireOp",EDGE,"E52")])],"isStart":true})],"blendedInto":[]});
            var Q30;
            Q30=makeQuery(id+"F3.opFillet","BLEND_EDGE",EDGE,{"blendedFrom":[makeQuery(id+"F1.opExtrude","CAP_EDGE",EDGE,{"disambiguationData":[OSD([sQuery(id+"F0.wireOp",EDGE,"E52")])],"isStart":true}),makeQuery(id+"F1.opExtrude","CAP_EDGE",EDGE,{"disambiguationData":[OSD([sQuery(id+"F0.wireOp",EDGE,"E53")])],"isStart":true})],"blendedInto":[]});
            var Q31;
            Q31=makeQuery(id+"F3.opFillet","BLEND_EDGE",EDGE,{"blendedFrom":[makeQuery(id+"F1.opExtrude","CAP_EDGE",EDGE,{"disambiguationData":[OSD([sQuery(id+"F0.wireOp",EDGE,"E53")])],"isStart":true}),makeQuery(id+"F1.opExtrude","CAP_EDGE",EDGE,{"disambiguationData":[OSD([sQuery(id+"F0.wireOp",EDGE,"E54")])],"isStart":true})],"blendedInto":[]});
            var Q32;
            Q32=makeQuery(id+"F3.opFillet","BLEND_EDGE",EDGE,{"blendedFrom":[makeQuery(id+"F1.opExtrude","CAP_EDGE",EDGE,{"disambiguationData":[OSD([sQuery(id+"F0.wireOp",EDGE,"E54")])],"isStart":true}),makeQuery(id+"F1.opExtrude","CAP_EDGE",EDGE,{"disambiguationData":[OSD([sQuery(id+"F0.wireOp",EDGE,"E55")])],"isStart":true})],"blendedInto":[]});
            var Q33;
            Q33=makeQuery(id+"F3.opFillet","BLEND_EDGE",EDGE,{"blendedFrom":[makeQuery(id+"F1.opExtrude","CAP_EDGE",EDGE,{"disambiguationData":[OSD([sQuery(id+"F0.wireOp",EDGE,"E55")])],"isStart":true}),makeQuery(id+"F1.opExtrude","CAP_EDGE",EDGE,{"disambiguationData":[OSD([sQuery(id+"F0.wireOp",EDGE,"E56")])],"isStart":true})],"blendedInto":[]});
            var Q34;
            Q34=makeQuery(id+"F3.opFillet","BLEND_EDGE",EDGE,{"blendedFrom":[makeQuery(id+"F1.opExtrude","CAP_EDGE",EDGE,{"disambiguationData":[OSD([sQuery(id+"F0.wireOp",EDGE,"E56")])],"isStart":true}),makeQuery(id+"F1.opExtrude","CAP_EDGE",EDGE,{"disambiguationData":[OSD([sQuery(id+"F0.wireOp",EDGE,"E57")])],"isStart":true})],"blendedInto":[]});
            var Q35;
            Q35=makeQuery(id+"F3.opFillet","BLEND_EDGE",EDGE,{"blendedFrom":[makeQuery(id+"F1.opExtrude","CAP_EDGE",EDGE,{"disambiguationData":[OSD([sQuery(id+"F0.wireOp",EDGE,"E57")])],"isStart":true}),makeQuery(id+"F1.opExtrude","CAP_EDGE",EDGE,{"disambiguationData":[OSD([sQuery(id+"F0.wireOp",EDGE,"E58")])],"isStart":true})],"blendedInto":[]});
            var Q36;
            Q36=makeQuery(id+"F3.opFillet","BLEND_EDGE",EDGE,{"blendedFrom":[makeQuery(id+"F1.opExtrude","CAP_EDGE",EDGE,{"disambiguationData":[OSD([sQuery(id+"F0.wireOp",EDGE,"E58")])],"isStart":true}),makeQuery(id+"F1.opExtrude","CAP_EDGE",EDGE,{"disambiguationData":[OSD([sQuery(id+"F0.wireOp",EDGE,"E59")])],"isStart":true})],"blendedInto":[]});
            var Q37;
            Q37=makeQuery(id+"F3.opFillet","BLEND_EDGE",EDGE,{"blendedFrom":[makeQuery(id+"F1.opExtrude","CAP_EDGE",EDGE,{"disambiguationData":[OSD([sQuery(id+"F0.wireOp",EDGE,"E59")])],"isStart":true}),makeQuery(id+"F1.opExtrude","CAP_EDGE",EDGE,{"disambiguationData":[OSD([sQuery(id+"F0.wireOp",EDGE,"E60")])],"isStart":true})],"blendedInto":[]});
            var Q38;
            Q38=makeQuery(id+"F3.opFillet","BLEND_EDGE",EDGE,{"blendedFrom":[makeQuery(id+"F1.opExtrude","CAP_EDGE",EDGE,{"disambiguationData":[OSD([sQuery(id+"F0.wireOp",EDGE,"E60")])],"isStart":true}),makeQuery(id+"F1.opExtrude","CAP_EDGE",EDGE,{"disambiguationData":[OSD([sQuery(id+"F0.wireOp",EDGE,"E61")])],"isStart":true})],"blendedInto":[]});
            var Q39;
            Q39=makeQuery(id+"F3.opFillet","BLEND_EDGE",EDGE,{"blendedFrom":[makeQuery(id+"F1.opExtrude","CAP_EDGE",EDGE,{"disambiguationData":[OSD([sQuery(id+"F0.wireOp",EDGE,"E61")])],"isStart":true}),makeQuery(id+"F1.opExtrude","CAP_EDGE",EDGE,{"disambiguationData":[OSD([sQuery(id+"F0.wireOp",EDGE,"E62")])],"isStart":true})],"blendedInto":[]});
            var Q40;
            Q40=makeQuery(id+"F3.opFillet","BLEND_EDGE",EDGE,{"blendedFrom":[makeQuery(id+"F1.opExtrude","CAP_EDGE",EDGE,{"disambiguationData":[OSD([sQuery(id+"F0.wireOp",EDGE,"E62")])],"isStart":true}),makeQuery(id+"F1.opExtrude","CAP_EDGE",EDGE,{"disambiguationData":[OSD([sQuery(id+"F0.wireOp",EDGE,"E63")])],"isStart":true})],"blendedInto":[]});
            var Q41;
            Q41=makeQuery(id+"F3.opFillet","BLEND_EDGE",EDGE,{"blendedFrom":[makeQuery(id+"F1.opExtrude","CAP_EDGE",EDGE,{"disambiguationData":[OSD([sQuery(id+"F0.wireOp",EDGE,"E63")])],"isStart":true}),makeQuery(id+"F1.opExtrude","CAP_EDGE",EDGE,{"disambiguationData":[OSD([sQuery(id+"F0.wireOp",EDGE,"E64")])],"isStart":true})],"blendedInto":[]});
            var Q42;
            Q42=makeQuery(id+"F3.opFillet","BLEND_EDGE",EDGE,{"blendedFrom":[makeQuery(id+"F1.opExtrude","CAP_EDGE",EDGE,{"disambiguationData":[OSD([sQuery(id+"F0.wireOp",EDGE,"E1")])],"isStart":true}),makeQuery(id+"F1.opExtrude","CAP_EDGE",EDGE,{"disambiguationData":[OSD([sQuery(id+"F0.wireOp",EDGE,"E64")])],"isStart":true})],"blendedInto":[]});
            var Q43;
            Q43=makeQuery(id+"F3.opFillet","BLEND_EDGE",EDGE,{"blendedFrom":[makeQuery(id+"F1.opExtrude","CAP_EDGE",EDGE,{"disambiguationData":[OSD([sQuery(id+"F0.wireOp",EDGE,"E1")])],"isStart":true}),makeQuery(id+"F1.opExtrude","CAP_EDGE",EDGE,{"disambiguationData":[OSD([sQuery(id+"F0.wireOp",EDGE,"E2")])],"isStart":true})],"blendedInto":[]});
            var Q44;
            Q44=makeQuery(id+"F3.opFillet","BLEND_EDGE",EDGE,{"blendedFrom":[makeQuery(id+"F1.opExtrude","CAP_EDGE",EDGE,{"disambiguationData":[OSD([sQuery(id+"F0.wireOp",EDGE,"E2")])],"isStart":true}),makeQuery(id+"F1.opExtrude","CAP_EDGE",EDGE,{"disambiguationData":[OSD([sQuery(id+"F0.wireOp",EDGE,"E3")])],"isStart":true})],"blendedInto":[]});
            var Q45;
            Q45=makeQuery(id+"F3.opFillet","BLEND_EDGE",EDGE,{"blendedFrom":[makeQuery(id+"F1.opExtrude","CAP_EDGE",EDGE,{"disambiguationData":[OSD([sQuery(id+"F0.wireOp",EDGE,"E3")])],"isStart":true}),makeQuery(id+"F1.opExtrude","CAP_EDGE",EDGE,{"disambiguationData":[OSD([sQuery(id+"F0.wireOp",EDGE,"E4")])],"isStart":true})],"blendedInto":[]});
            var Q46;
            Q46=makeQuery(id+"F3.opFillet","BLEND_EDGE",EDGE,{"blendedFrom":[makeQuery(id+"F1.opExtrude","CAP_EDGE",EDGE,{"disambiguationData":[OSD([sQuery(id+"F0.wireOp",EDGE,"E4")])],"isStart":true}),makeQuery(id+"F1.opExtrude","CAP_EDGE",EDGE,{"disambiguationData":[OSD([sQuery(id+"F0.wireOp",EDGE,"E5")])],"isStart":true})],"blendedInto":[]});
            var Q47;
            Q47=makeQuery(id+"F3.opFillet","BLEND_EDGE",EDGE,{"blendedFrom":[makeQuery(id+"F1.opExtrude","CAP_EDGE",EDGE,{"disambiguationData":[OSD([sQuery(id+"F0.wireOp",EDGE,"E5")])],"isStart":true}),makeQuery(id+"F1.opExtrude","CAP_EDGE",EDGE,{"disambiguationData":[OSD([sQuery(id+"F0.wireOp",EDGE,"E6")])],"isStart":true})],"blendedInto":[]});
            var Q48;
            Q48=makeQuery(id+"F3.opFillet","BLEND_EDGE",EDGE,{"blendedFrom":[makeQuery(id+"F1.opExtrude","CAP_EDGE",EDGE,{"disambiguationData":[OSD([sQuery(id+"F0.wireOp",EDGE,"E6")])],"isStart":true}),makeQuery(id+"F1.opExtrude","CAP_EDGE",EDGE,{"disambiguationData":[OSD([sQuery(id+"F0.wireOp",EDGE,"E7")])],"isStart":true})],"blendedInto":[]});
            var Q49;
            Q49=makeQuery(id+"F3.opFillet","BLEND_EDGE",EDGE,{"blendedFrom":[makeQuery(id+"F1.opExtrude","CAP_EDGE",EDGE,{"disambiguationData":[OSD([sQuery(id+"F0.wireOp",EDGE,"E7")])],"isStart":true}),makeQuery(id+"F1.opExtrude","CAP_EDGE",EDGE,{"disambiguationData":[OSD([sQuery(id+"F0.wireOp",EDGE,"E8")])],"isStart":true})],"blendedInto":[]});
            var Q50;
            Q50=makeQuery(id+"F3.opFillet","BLEND_EDGE",EDGE,{"blendedFrom":[makeQuery(id+"F1.opExtrude","CAP_EDGE",EDGE,{"disambiguationData":[OSD([sQuery(id+"F0.wireOp",EDGE,"E8")])],"isStart":true}),makeQuery(id+"F1.opExtrude","CAP_EDGE",EDGE,{"disambiguationData":[OSD([sQuery(id+"F0.wireOp",EDGE,"E9")])],"isStart":true})],"blendedInto":[]});
            var Q51;
            Q51=makeQuery(id+"F3.opFillet","BLEND_EDGE",EDGE,{"blendedFrom":[makeQuery(id+"F1.opExtrude","CAP_EDGE",EDGE,{"disambiguationData":[OSD([sQuery(id+"F0.wireOp",EDGE,"E9")])],"isStart":true}),makeQuery(id+"F1.opExtrude","CAP_EDGE",EDGE,{"disambiguationData":[OSD([sQuery(id+"F0.wireOp",EDGE,"E10")])],"isStart":true})],"blendedInto":[]});
            var Q52;
            Q52=makeQuery(id+"F3.opFillet","BLEND_EDGE",EDGE,{"blendedFrom":[makeQuery(id+"F1.opExtrude","CAP_EDGE",EDGE,{"disambiguationData":[OSD([sQuery(id+"F0.wireOp",EDGE,"E10")])],"isStart":true}),makeQuery(id+"F1.opExtrude","CAP_EDGE",EDGE,{"disambiguationData":[OSD([sQuery(id+"F0.wireOp",EDGE,"E11")])],"isStart":true})],"blendedInto":[]});
            var Q53;
            Q53=makeQuery(id+"F3.opFillet","BLEND_EDGE",EDGE,{"blendedFrom":[makeQuery(id+"F1.opExtrude","CAP_EDGE",EDGE,{"disambiguationData":[OSD([sQuery(id+"F0.wireOp",EDGE,"E11")])],"isStart":true}),makeQuery(id+"F1.opExtrude","CAP_EDGE",EDGE,{"disambiguationData":[OSD([sQuery(id+"F0.wireOp",EDGE,"E12")])],"isStart":true})],"blendedInto":[]});
            var Q54;
            Q54=makeQuery(id+"F3.opFillet","BLEND_EDGE",EDGE,{"blendedFrom":[makeQuery(id+"F1.opExtrude","CAP_EDGE",EDGE,{"disambiguationData":[OSD([sQuery(id+"F0.wireOp",EDGE,"E12")])],"isStart":true}),makeQuery(id+"F1.opExtrude","CAP_EDGE",EDGE,{"disambiguationData":[OSD([sQuery(id+"F0.wireOp",EDGE,"E13")])],"isStart":true})],"blendedInto":[]});
            var Q55;
            Q55=makeQuery(id+"F3.opFillet","BLEND_EDGE",EDGE,{"blendedFrom":[makeQuery(id+"F1.opExtrude","CAP_EDGE",EDGE,{"disambiguationData":[OSD([sQuery(id+"F0.wireOp",EDGE,"E13")])],"isStart":true}),makeQuery(id+"F1.opExtrude","CAP_EDGE",EDGE,{"disambiguationData":[OSD([sQuery(id+"F0.wireOp",EDGE,"E14")])],"isStart":true})],"blendedInto":[]});
            var Q56;
            Q56=makeQuery(id+"F3.opFillet","BLEND_EDGE",EDGE,{"blendedFrom":[makeQuery(id+"F1.opExtrude","CAP_EDGE",EDGE,{"disambiguationData":[OSD([sQuery(id+"F0.wireOp",EDGE,"E14")])],"isStart":true}),makeQuery(id+"F1.opExtrude","CAP_EDGE",EDGE,{"disambiguationData":[OSD([sQuery(id+"F0.wireOp",EDGE,"E15")])],"isStart":true})],"blendedInto":[]});
            var Q57;
            Q57=makeQuery(id+"F3.opFillet","BLEND_EDGE",EDGE,{"blendedFrom":[makeQuery(id+"F1.opExtrude","CAP_EDGE",EDGE,{"disambiguationData":[OSD([sQuery(id+"F0.wireOp",EDGE,"E15")])],"isStart":true}),makeQuery(id+"F1.opExtrude","CAP_EDGE",EDGE,{"disambiguationData":[OSD([sQuery(id+"F0.wireOp",EDGE,"E16")])],"isStart":true})],"blendedInto":[]});
            var Q58;
            Q58=makeQuery(id+"F3.opFillet","BLEND_EDGE",EDGE,{"blendedFrom":[makeQuery(id+"F1.opExtrude","CAP_EDGE",EDGE,{"disambiguationData":[OSD([sQuery(id+"F0.wireOp",EDGE,"E16")])],"isStart":true}),makeQuery(id+"F1.opExtrude","CAP_EDGE",EDGE,{"disambiguationData":[OSD([sQuery(id+"F0.wireOp",EDGE,"E17")])],"isStart":true})],"blendedInto":[]});
            var Q59;
            Q59=makeQuery(id+"F3.opFillet","BLEND_EDGE",EDGE,{"blendedFrom":[makeQuery(id+"F1.opExtrude","CAP_EDGE",EDGE,{"disambiguationData":[OSD([sQuery(id+"F0.wireOp",EDGE,"E17")])],"isStart":true}),makeQuery(id+"F1.opExtrude","CAP_EDGE",EDGE,{"disambiguationData":[OSD([sQuery(id+"F0.wireOp",EDGE,"E18")])],"isStart":true})],"blendedInto":[]});
            var Q60;
            Q60=makeQuery(id+"F3.opFillet","BLEND_EDGE",EDGE,{"blendedFrom":[makeQuery(id+"F1.opExtrude","CAP_EDGE",EDGE,{"disambiguationData":[OSD([sQuery(id+"F0.wireOp",EDGE,"E18")])],"isStart":true}),makeQuery(id+"F1.opExtrude","CAP_EDGE",EDGE,{"disambiguationData":[OSD([sQuery(id+"F0.wireOp",EDGE,"E19")])],"isStart":true})],"blendedInto":[]});
            var Q61;
            Q61=makeQuery(id+"F3.opFillet","BLEND_EDGE",EDGE,{"blendedFrom":[makeQuery(id+"F1.opExtrude","CAP_EDGE",EDGE,{"disambiguationData":[OSD([sQuery(id+"F0.wireOp",EDGE,"E19")])],"isStart":true}),makeQuery(id+"F1.opExtrude","CAP_EDGE",EDGE,{"disambiguationData":[OSD([sQuery(id+"F0.wireOp",EDGE,"E20")])],"isStart":true})],"blendedInto":[]});
            var Q62;
            Q62=makeQuery(id+"F3.opFillet","BLEND_EDGE",EDGE,{"blendedFrom":[makeQuery(id+"F1.opExtrude","CAP_EDGE",EDGE,{"disambiguationData":[OSD([sQuery(id+"F0.wireOp",EDGE,"E20")])],"isStart":true}),makeQuery(id+"F1.opExtrude","CAP_EDGE",EDGE,{"disambiguationData":[OSD([sQuery(id+"F0.wireOp",EDGE,"E21")])],"isStart":true})],"blendedInto":[]});
            var Q63;
            Q63=makeQuery(id+"F3.opFillet","BLEND_EDGE",EDGE,{"blendedFrom":[makeQuery(id+"F1.opExtrude","CAP_EDGE",EDGE,{"disambiguationData":[OSD([sQuery(id+"F0.wireOp",EDGE,"E21")])],"isStart":true}),makeQuery(id+"F1.opExtrude","CAP_EDGE",EDGE,{"disambiguationData":[OSD([sQuery(id+"F0.wireOp",EDGE,"E22")])],"isStart":true})],"blendedInto":[]});
            fillet(context, id + "F4", {"entities" : qUnion([Q0, Q1, Q2, Q3, Q4, Q5, Q6, Q7, Q8, Q9, Q10, Q11, Q12, Q13, Q14, Q15, Q16, Q17, Q18, Q19, Q20, Q21, Q22, Q23, Q24, Q25, Q26, Q27, Q28, Q29, Q30, Q31, Q32, Q33, Q34, Q35, Q36, Q37, Q38, Q39, Q40, Q41, Q42, Q43, Q44, Q45, Q46, Q47, Q48, Q49, Q50, Q51, Q52, Q53, Q54, Q55, Q56, Q57, Q58, Q59, Q60, Q61, Q62, Q63]), "radius" : 3 * mm, "tangentPropagation" : true, "allowEdgeOverflow" : false});
        }
        {
            var Q0;
            Q0=makeQuery(id+"F1.opExtrude","SWEPT_BODY",BODY,{"disambiguationData":[OSD([sQuery(id+"F0.wireOp",EDGE,"E1"),sQuery(id+"F0.wireOp",EDGE,"E2"),sQuery(id+"F0.wireOp",EDGE,"E3"),sQuery(id+"F0.wireOp",EDGE,"E4"),sQuery(id+"F0.wireOp",EDGE,"E5"),sQuery(id+"F0.wireOp",EDGE,"E6"),sQuery(id+"F0.wireOp",EDGE,"E7"),sQuery(id+"F0.wireOp",EDGE,"E8"),sQuery(id+"F0.wireOp",EDGE,"E9"),sQuery(id+"F0.wireOp",EDGE,"E10"),sQuery(id+"F0.wireOp",EDGE,"E11"),sQuery(id+"F0.wireOp",EDGE,"E12"),sQuery(id+"F0.wireOp",EDGE,"E13"),sQuery(id+"F0.wireOp",EDGE,"E14"),sQuery(id+"F0.wireOp",EDGE,"E15"),sQuery(id+"F0.wireOp",EDGE,"E16"),sQuery(id+"F0.wireOp",EDGE,"E17"),sQuery(id+"F0.wireOp",EDGE,"E18"),sQuery(id+"F0.wireOp",EDGE,"E19"),sQuery(id+"F0.wireOp",EDGE,"E20"),sQuery(id+"F0.wireOp",EDGE,"E21"),sQuery(id+"F0.wireOp",EDGE,"E22"),sQuery(id+"F0.wireOp",EDGE,"E23"),sQuery(id+"F0.wireOp",EDGE,"E24"),sQuery(id+"F0.wireOp",EDGE,"E25"),sQuery(id+"F0.wireOp",EDGE,"E26"),sQuery(id+"F0.wireOp",EDGE,"E27"),sQuery(id+"F0.wireOp",EDGE,"E28"),sQuery(id+"F0.wireOp",EDGE,"E29"),sQuery(id+"F0.wireOp",EDGE,"E30"),sQuery(id+"F0.wireOp",EDGE,"E31"),sQuery(id+"F0.wireOp",EDGE,"E32"),sQuery(id+"F0.wireOp",EDGE,"E33"),sQuery(id+"F0.wireOp",EDGE,"E34"),sQuery(id+"F0.wireOp",EDGE,"E35"),sQuery(id+"F0.wireOp",EDGE,"E36"),sQuery(id+"F0.wireOp",EDGE,"E37"),sQuery(id+"F0.wireOp",EDGE,"E38"),sQuery(id+"F0.wireOp",EDGE,"E39"),sQuery(id+"F0.wireOp",EDGE,"E40"),sQuery(id+"F0.wireOp",EDGE,"E41"),sQuery(id+"F0.wireOp",EDGE,"E42"),sQuery(id+"F0.wireOp",EDGE,"E43"),sQuery(id+"F0.wireOp",EDGE,"E44"),sQuery(id+"F0.wireOp",EDGE,"E45"),sQuery(id+"F0.wireOp",EDGE,"E46"),sQuery(id+"F0.wireOp",EDGE,"E47"),sQuery(id+"F0.wireOp",EDGE,"E48"),sQuery(id+"F0.wireOp",EDGE,"E49"),sQuery(id+"F0.wireOp",EDGE,"E50"),sQuery(id+"F0.wireOp",EDGE,"E51"),sQuery(id+"F0.wireOp",EDGE,"E52"),sQuery(id+"F0.wireOp",EDGE,"E53"),sQuery(id+"F0.wireOp",EDGE,"E54"),sQuery(id+"F0.wireOp",EDGE,"E55"),sQuery(id+"F0.wireOp",EDGE,"E56"),sQuery(id+"F0.wireOp",EDGE,"E57"),sQuery(id+"F0.wireOp",EDGE,"E58"),sQuery(id+"F0.wireOp",EDGE,"E59"),sQuery(id+"F0.wireOp",EDGE,"E60"),sQuery(id+"F0.wireOp",EDGE,"E61"),sQuery(id+"F0.wireOp",EDGE,"E62"),sQuery(id+"F0.wireOp",EDGE,"E63"),sQuery(id+"F0.wireOp",EDGE,"E64"),sQuery(id+"F0.wireOp",EDGE,"E66")])]});
            transform(context, id + "F5", {"entities" : qUnion([Q0]), "transformType" : TransformType.TRANSLATION_3D, "dx" : 0 * mm, "dy" : 0 * mm, "dz" : 0 * mm, "makeCopy" : true});
        }
        {
            var Q0;
            Q0=makeQuery(id+"F1.opExtrude","SWEPT_BODY",BODY,{"disambiguationData":[OSD([sQuery(id+"F0.wireOp",EDGE,"E1"),sQuery(id+"F0.wireOp",EDGE,"E2"),sQuery(id+"F0.wireOp",EDGE,"E3"),sQuery(id+"F0.wireOp",EDGE,"E4"),sQuery(id+"F0.wireOp",EDGE,"E5"),sQuery(id+"F0.wireOp",EDGE,"E6"),sQuery(id+"F0.wireOp",EDGE,"E7"),sQuery(id+"F0.wireOp",EDGE,"E8"),sQuery(id+"F0.wireOp",EDGE,"E9"),sQuery(id+"F0.wireOp",EDGE,"E10"),sQuery(id+"F0.wireOp",EDGE,"E11"),sQuery(id+"F0.wireOp",EDGE,"E12"),sQuery(id+"F0.wireOp",EDGE,"E13"),sQuery(id+"F0.wireOp",EDGE,"E14"),sQuery(id+"F0.wireOp",EDGE,"E15"),sQuery(id+"F0.wireOp",EDGE,"E16"),sQuery(id+"F0.wireOp",EDGE,"E17"),sQuery(id+"F0.wireOp",EDGE,"E18"),sQuery(id+"F0.wireOp",EDGE,"E19"),sQuery(id+"F0.wireOp",EDGE,"E20"),sQuery(id+"F0.wireOp",EDGE,"E21"),sQuery(id+"F0.wireOp",EDGE,"E22"),sQuery(id+"F0.wireOp",EDGE,"E23"),sQuery(id+"F0.wireOp",EDGE,"E24"),sQuery(id+"F0.wireOp",EDGE,"E25"),sQuery(id+"F0.wireOp",EDGE,"E26"),sQuery(id+"F0.wireOp",EDGE,"E27"),sQuery(id+"F0.wireOp",EDGE,"E28"),sQuery(id+"F0.wireOp",EDGE,"E29"),sQuery(id+"F0.wireOp",EDGE,"E30"),sQuery(id+"F0.wireOp",EDGE,"E31"),sQuery(id+"F0.wireOp",EDGE,"E32"),sQuery(id+"F0.wireOp",EDGE,"E33"),sQuery(id+"F0.wireOp",EDGE,"E34"),sQuery(id+"F0.wireOp",EDGE,"E35"),sQuery(id+"F0.wireOp",EDGE,"E36"),sQuery(id+"F0.wireOp",EDGE,"E37"),sQuery(id+"F0.wireOp",EDGE,"E38"),sQuery(id+"F0.wireOp",EDGE,"E39"),sQuery(id+"F0.wireOp",EDGE,"E40"),sQuery(id+"F0.wireOp",EDGE,"E41"),sQuery(id+"F0.wireOp",EDGE,"E42"),sQuery(id+"F0.wireOp",EDGE,"E43"),sQuery(id+"F0.wireOp",EDGE,"E44"),sQuery(id+"F0.wireOp",EDGE,"E45"),sQuery(id+"F0.wireOp",EDGE,"E46"),sQuery(id+"F0.wireOp",EDGE,"E47"),sQuery(id+"F0.wireOp",EDGE,"E48"),sQuery(id+"F0.wireOp",EDGE,"E49"),sQuery(id+"F0.wireOp",EDGE,"E50"),sQuery(id+"F0.wireOp",EDGE,"E51"),sQuery(id+"F0.wireOp",EDGE,"E52"),sQuery(id+"F0.wireOp",EDGE,"E53"),sQuery(id+"F0.wireOp",EDGE,"E54"),sQuery(id+"F0.wireOp",EDGE,"E55"),sQuery(id+"F0.wireOp",EDGE,"E56"),sQuery(id+"F0.wireOp",EDGE,"E57"),sQuery(id+"F0.wireOp",EDGE,"E58"),sQuery(id+"F0.wireOp",EDGE,"E59"),sQuery(id+"F0.wireOp",EDGE,"E60"),sQuery(id+"F0.wireOp",EDGE,"E61"),sQuery(id+"F0.wireOp",EDGE,"E62"),sQuery(id+"F0.wireOp",EDGE,"E63"),sQuery(id+"F0.wireOp",EDGE,"E64"),sQuery(id+"F0.wireOp",EDGE,"E66")])]});
            deleteBodies(context, id + "F6", {"entities" : qUnion([Q0])});
        }
    });
